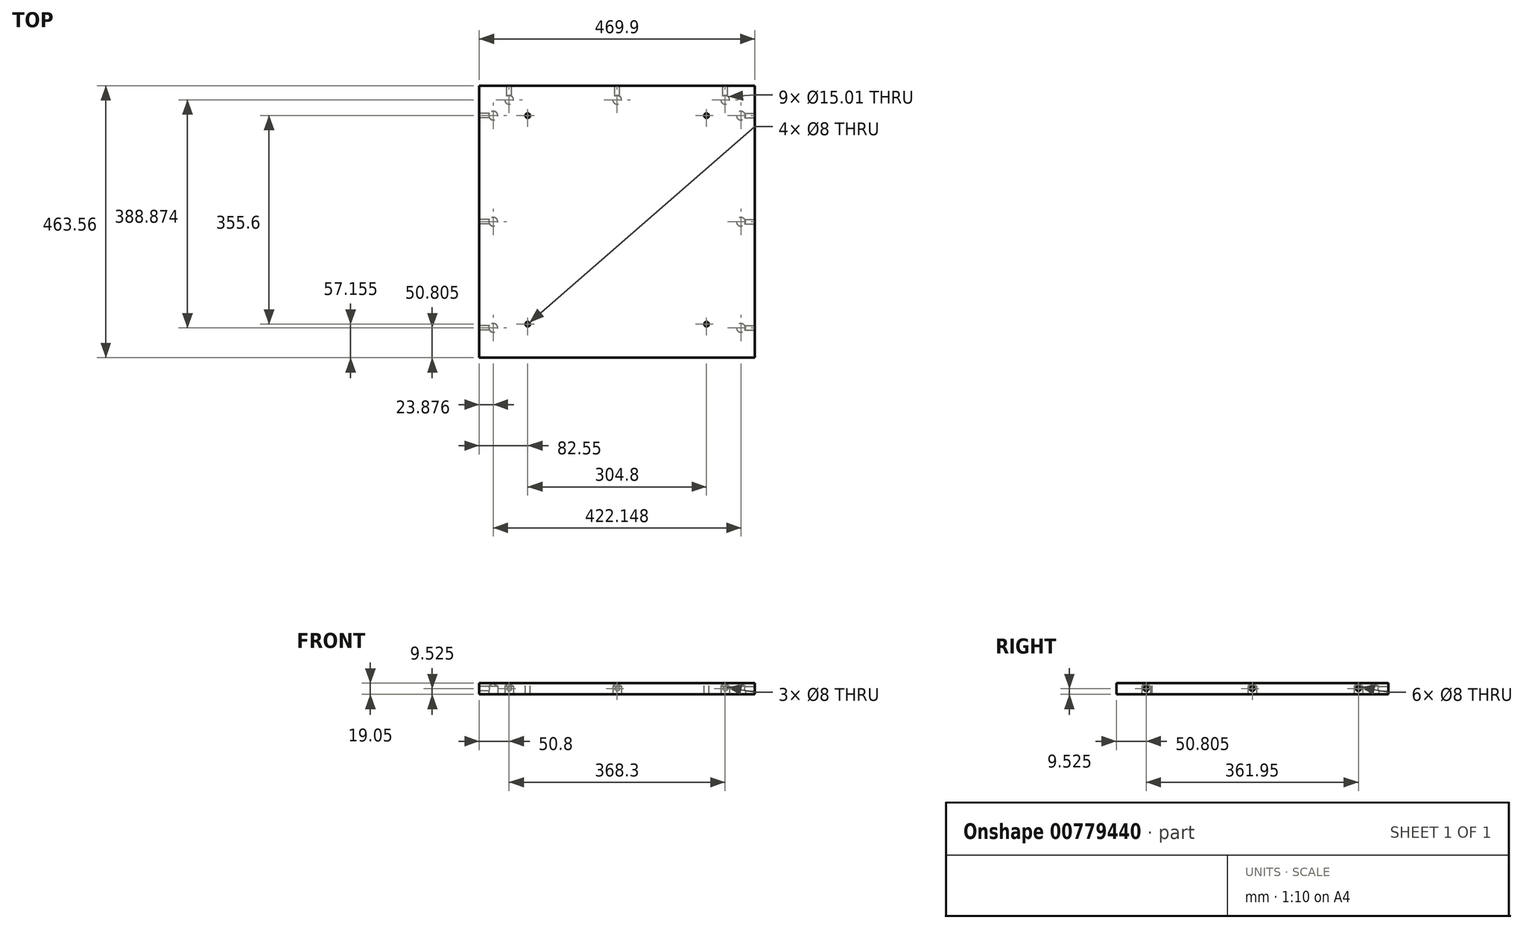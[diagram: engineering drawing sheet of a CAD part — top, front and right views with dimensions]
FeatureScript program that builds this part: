
annotation { "Feature Type Name" : "Feature", "Feature Type Description" : "" }
export const myFeature = defineFeature(function(context is Context, id is Id, definition is map)
    precondition{}
    {
        {
            var Q0;
            Q0=qCreatedBy(makeId("Top.planeOp"),FACE);
            var sketch = newSketch(context, id + "F0", { "sketchPlane" : qUnion([Q0])});
            skLineSegment(sketch, "E0.bottom", {"start": v(234.95, 231.78) * mm, "end": v(-234.95, 231.78) * mm});
            skLineSegment(sketch, "E0.top", {"start": v(234.95, -231.78) * mm, "end": v(-234.95, -231.78) * mm});
            skLineSegment(sketch, "E0.left", {"start": v(234.95, 231.77) * mm, "end": v(234.95, -231.78) * mm});
            skLineSegment(sketch, "E0.right", {"start": v(-234.95, 231.78) * mm, "end": v(-234.95, -231.78) * mm});
            skPoint(sketch, "E0.middle", {"position": v(0, 0) * mm});
            skSolve(sketch);
        }
        {
            var Q0;
            Q0=makeQuery(id+"F0.imprint","IMPRINT",FACE,{"disambiguationData":[TD([[makeQuery(id+"F0.imprint","IMPRINT",EDGE,{"derivedFrom":sQuery(id+"F0.wireOp",EDGE,"E0.bottom")}),1.0]])]});
            extrude(context, id + "F1", {"entities" : qUnion([Q0]), "depth" : 19.05 * mm, "offsetDistance" : 25.4 * mm});
        }
        {
            var Q0;
            Q0=makeQuery(id+"F1.opExtrude","CAP_FACE",FACE,{"disambiguationData":[OSD([sQuery(id+"F0.wireOp",EDGE,"E0.bottom"),sQuery(id+"F0.wireOp",EDGE,"E0.top"),sQuery(id+"F0.wireOp",EDGE,"E0.left"),sQuery(id+"F0.wireOp",EDGE,"E0.right")])],"isStart":true});
            var sketch = newSketch(context, id + "F2", { "sketchPlane" : qUnion([Q0])});
            skLineSegment(sketch, "E1", {"start": v(-234.95, 231.78) * mm, "end": v(-211.07, 231.78) * mm});
            skLineSegment(sketch, "E2", {"start": v(-211.07, 231.78) * mm, "end": v(-211.07, 180.97) * mm});
            skLineSegment(sketch, "E3", {"start": v(-234.95, -231.78) * mm, "end": v(-211.07, -231.78) * mm});
            skLineSegment(sketch, "E4", {"start": v(-211.07, -231.78) * mm, "end": v(-211.07, -180.97) * mm});
            skLineSegment(sketch, "E5", {"start": v(234.95, 231.78) * mm, "end": v(234.95, 207.9) * mm});
            skLineSegment(sketch, "E6", {"start": v(234.95, 231.78) * mm, "end": v(211.07, 231.78) * mm});
            skLineSegment(sketch, "E7", {"start": v(211.07, 231.78) * mm, "end": v(211.07, 180.97) * mm});
            skLineSegment(sketch, "E8", {"start": v(234.95, -231.78) * mm, "end": v(211.07, -231.78) * mm});
            skLineSegment(sketch, "E9", {"start": v(211.07, -231.78) * mm, "end": v(211.07, -180.97) * mm});
            skLineSegment(sketch, "E10", {"start": v(-234.95, 0) * mm, "end": v(-211.07, 0) * mm});
            skLineSegment(sketch, "E11", {"start": v(234.95, 0) * mm, "end": v(211.07, 0) * mm});
            skLineSegment(sketch, "E12", {"start": v(0, -231.78) * mm, "end": v(0, -207.9) * mm});
            skLineSegment(sketch, "E13", {"start": v(-234.95, -231.78) * mm, "end": v(-234.95, -207.9) * mm});
            skLineSegment(sketch, "E14", {"start": v(-234.95, -207.9) * mm, "end": v(-184.15, -207.9) * mm});
            skLineSegment(sketch, "E15", {"start": v(234.95, -231.78) * mm, "end": v(234.95, -207.9) * mm});
            skLineSegment(sketch, "E16", {"start": v(234.95, -207.9) * mm, "end": v(184.15, -207.9) * mm});
            skPoint(sketch, "E17", {"position": v(-211.07, 180.97) * mm});
            skPoint(sketch, "E18", {"position": v(211.07, 180.97) * mm});
            skPoint(sketch, "E19", {"position": v(211.07, 0) * mm});
            skPoint(sketch, "E20", {"position": v(-211.07, 0) * mm});
            skPoint(sketch, "E21", {"position": v(-211.07, -180.97) * mm});
            skPoint(sketch, "E22", {"position": v(-184.15, -207.9) * mm});
            skPoint(sketch, "E23", {"position": v(0, -207.9) * mm});
            skPoint(sketch, "E24", {"position": v(184.15, -207.9) * mm});
            skPoint(sketch, "E25", {"position": v(211.07, -180.97) * mm});
            skSolve(sketch);
        }
        {
            var Q0;
            Q0=sQuery(id+"F2.wireOp",VERTEX,"E17");
            var Q1;
            Q1=sQuery(id+"F2.wireOp",VERTEX,"E20");
            var Q2;
            Q2=sQuery(id+"F2.wireOp",VERTEX,"E21");
            var Q3;
            Q3=sQuery(id+"F2.wireOp",VERTEX,"E22");
            var Q4;
            Q4=sQuery(id+"F2.wireOp",VERTEX,"E23");
            var Q5;
            Q5=sQuery(id+"F2.wireOp",VERTEX,"E24");
            var Q6;
            Q6=sQuery(id+"F2.wireOp",VERTEX,"E25");
            var Q7;
            Q7=sQuery(id+"F2.wireOp",VERTEX,"E19");
            var Q8;
            Q8=sQuery(id+"F2.wireOp",VERTEX,"E18");
            var Q9;
            Q9=makeQuery(id+"F1.opExtrude","SWEPT_BODY",BODY,{"disambiguationData":[OSD([sQuery(id+"F0.wireOp",EDGE,"E0.bottom"),sQuery(id+"F0.wireOp",EDGE,"E0.top"),sQuery(id+"F0.wireOp",EDGE,"E0.left"),sQuery(id+"F0.wireOp",EDGE,"E0.right")])]});
            hole(context, id + "F3", {"style" : HoleStyle.SIMPLE, "endStyle" : HoleEndStyle.BLIND, "holeDiameter" : 15 * mm, "majorDiameter" : 6.35 * mm, "holeDepth" : 14.22 * mm, "isTappedThrough" : true, "tappedDepth" : 12.7 * mm, "tapClearance" : 3, "startFromSketch" : true, "locations" : qUnion([Q0, Q1, Q2, Q3, Q4, Q5, Q6, Q7, Q8]), "scope" : qUnion([Q9])});
        }
        {
            var Q0;
            Q0=makeQuery(id+"F1.opExtrude","SWEPT_FACE",FACE,{"disambiguationData":[OSD([sQuery(id+"F0.wireOp",EDGE,"E0.left")])]});
            var sketch = newSketch(context, id + "F4", { "sketchPlane" : qUnion([Q0])});
            skLineSegment(sketch, "E26", {"start": v(-231.77, 9.53) * mm, "end": v(-180.97, 9.53) * mm});
            skLineSegment(sketch, "E27", {"start": v(231.78, 9.53) * mm, "end": v(180.98, 9.53) * mm});
            skLineSegment(sketch, "E28", {"start": v(0, 19.05) * mm, "end": v(0, 9.53) * mm});
            skPoint(sketch, "E29", {"position": v(-180.97, 9.53) * mm});
            skPoint(sketch, "E30", {"position": v(0, 9.53) * mm});
            skPoint(sketch, "E31", {"position": v(180.98, 9.53) * mm});
            skSolve(sketch);
        }
        {
            var Q0;
            Q0=sQuery(id+"F4.wireOp",VERTEX,"E29");
            var Q1;
            Q1=sQuery(id+"F4.wireOp",VERTEX,"E30");
            var Q2;
            Q2=sQuery(id+"F4.wireOp",VERTEX,"E31");
            var Q3;
            Q3=makeQuery(id+"F1.opExtrude","SWEPT_BODY",BODY,{"disambiguationData":[OSD([sQuery(id+"F0.wireOp",EDGE,"E0.bottom"),sQuery(id+"F0.wireOp",EDGE,"E0.top"),sQuery(id+"F0.wireOp",EDGE,"E0.left"),sQuery(id+"F0.wireOp",EDGE,"E0.right")])]});
            hole(context, id + "F5", {"style" : HoleStyle.SIMPLE, "endStyle" : HoleEndStyle.BLIND, "holeDiameter" : 8 * mm, "majorDiameter" : 6.35 * mm, "holeDepth" : 25.4 * mm, "isTappedThrough" : true, "tappedDepth" : 12.7 * mm, "tapClearance" : 3, "startFromSketch" : true, "locations" : qUnion([Q0, Q1, Q2]), "scope" : qUnion([Q3])});
        }
        {
            var Q0;
            Q0=makeQuery(id+"F1.opExtrude","SWEPT_FACE",FACE,{"disambiguationData":[OSD([sQuery(id+"F0.wireOp",EDGE,"E0.bottom")])]});
            var sketch = newSketch(context, id + "F6", { "sketchPlane" : qUnion([Q0])});
            skLineSegment(sketch, "E32", {"start": v(-234.95, 9.53) * mm, "end": v(-184.15, 9.53) * mm});
            skLineSegment(sketch, "E33", {"start": v(234.95, 9.53) * mm, "end": v(184.15, 9.53) * mm});
            skLineSegment(sketch, "E34", {"start": v(0, 19.05) * mm, "end": v(0, 9.53) * mm});
            skPoint(sketch, "E35", {"position": v(-184.15, 9.53) * mm});
            skPoint(sketch, "E36", {"position": v(0, 9.53) * mm});
            skPoint(sketch, "E37", {"position": v(184.15, 9.53) * mm});
            skSolve(sketch);
        }
        {
            var Q0;
            Q0=sQuery(id+"F6.wireOp",VERTEX,"E35");
            var Q1;
            Q1=sQuery(id+"F6.wireOp",VERTEX,"E36");
            var Q2;
            Q2=sQuery(id+"F6.wireOp",VERTEX,"E37");
            var Q3;
            Q3=makeQuery(id+"F1.opExtrude","SWEPT_BODY",BODY,{"disambiguationData":[OSD([sQuery(id+"F0.wireOp",EDGE,"E0.bottom"),sQuery(id+"F0.wireOp",EDGE,"E0.top"),sQuery(id+"F0.wireOp",EDGE,"E0.left"),sQuery(id+"F0.wireOp",EDGE,"E0.right")])]});
            hole(context, id + "F7", {"style" : HoleStyle.SIMPLE, "endStyle" : HoleEndStyle.BLIND, "holeDiameter" : 8 * mm, "majorDiameter" : 6.35 * mm, "holeDepth" : 25.4 * mm, "isTappedThrough" : true, "tappedDepth" : 12.7 * mm, "tapClearance" : 3, "startFromSketch" : true, "locations" : qUnion([Q0, Q1, Q2]), "scope" : qUnion([Q3])});
        }
        {
            var Q0;
            Q0=makeQuery(id+"F1.opExtrude","SWEPT_FACE",FACE,{"disambiguationData":[OSD([sQuery(id+"F0.wireOp",EDGE,"E0.right")])]});
            var sketch = newSketch(context, id + "F8", { "sketchPlane" : qUnion([Q0])});
            skLineSegment(sketch, "E38", {"start": v(-231.77, 9.53) * mm, "end": v(-180.97, 9.53) * mm});
            skLineSegment(sketch, "E39", {"start": v(231.78, 9.53) * mm, "end": v(180.98, 9.53) * mm});
            skLineSegment(sketch, "E40", {"start": v(0, 19.05) * mm, "end": v(0, 9.53) * mm});
            skPoint(sketch, "E41", {"position": v(-180.97, 9.53) * mm});
            skPoint(sketch, "E42", {"position": v(0, 9.53) * mm});
            skPoint(sketch, "E43", {"position": v(180.98, 9.53) * mm});
            skSolve(sketch);
        }
        {
            var Q0;
            Q0=sQuery(id+"F8.wireOp",VERTEX,"E41");
            var Q1;
            Q1=sQuery(id+"F8.wireOp",VERTEX,"E42");
            var Q2;
            Q2=sQuery(id+"F8.wireOp",VERTEX,"E43");
            var Q3;
            Q3=makeQuery(id+"F1.opExtrude","SWEPT_BODY",BODY,{"disambiguationData":[OSD([sQuery(id+"F0.wireOp",EDGE,"E0.bottom"),sQuery(id+"F0.wireOp",EDGE,"E0.top"),sQuery(id+"F0.wireOp",EDGE,"E0.left"),sQuery(id+"F0.wireOp",EDGE,"E0.right")])]});
            hole(context, id + "F9", {"style" : HoleStyle.SIMPLE, "endStyle" : HoleEndStyle.BLIND, "holeDiameter" : 8 * mm, "majorDiameter" : 6.35 * mm, "holeDepth" : 25.4 * mm, "isTappedThrough" : true, "tappedDepth" : 12.7 * mm, "tapClearance" : 3, "startFromSketch" : true, "locations" : qUnion([Q0, Q1, Q2]), "scope" : qUnion([Q3])});
        }
        {
            var Q0;
            Q0=makeQuery(id+"F1.opExtrude","CAP_FACE",FACE,{"disambiguationData":[OSD([sQuery(id+"F0.wireOp",EDGE,"E0.bottom"),sQuery(id+"F0.wireOp",EDGE,"E0.top"),sQuery(id+"F0.wireOp",EDGE,"E0.left"),sQuery(id+"F0.wireOp",EDGE,"E0.right")])],"isStart":false});
            var sketch = newSketch(context, id + "F10", { "sketchPlane" : qUnion([Q0])});
            skLineSegment(sketch, "E44", {"start": v(0, 231.78) * mm, "end": v(0, 180.97) * mm});
            skLineSegment(sketch, "E45.bottom", {"start": v(0, 180.97) * mm, "end": v(-152.4, 180.97) * mm});
            skLineSegment(sketch, "E45.top", {"start": v(0, -174.63) * mm, "end": v(-152.4, -174.63) * mm});
            skLineSegment(sketch, "E45.left", {"start": v(0, 180.97) * mm, "end": v(0, -174.63) * mm});
            skLineSegment(sketch, "E45.right", {"start": v(-152.4, 180.97) * mm, "end": v(-152.4, -174.63) * mm});
            skLineSegment(sketch, "E46.bottom", {"start": v(0, 180.97) * mm, "end": v(152.4, 180.97) * mm});
            skLineSegment(sketch, "E46.top", {"start": v(0, -174.63) * mm, "end": v(152.4, -174.63) * mm});
            skLineSegment(sketch, "E46.right", {"start": v(152.4, 180.97) * mm, "end": v(152.4, -174.62) * mm});
            skPoint(sketch, "E47", {"position": v(-152.4, 180.97) * mm});
            skPoint(sketch, "E48", {"position": v(152.4, 180.97) * mm});
            skPoint(sketch, "E49", {"position": v(152.4, -174.63) * mm});
            skPoint(sketch, "E50", {"position": v(-152.4, -174.63) * mm});
            skSolve(sketch);
        }
        {
            var Q0;
            Q0=sQuery(id+"F10.wireOp",VERTEX,"E47");
            var Q1;
            Q1=sQuery(id+"F10.wireOp",VERTEX,"E48");
            var Q2;
            Q2=sQuery(id+"F10.wireOp",VERTEX,"E49");
            var Q3;
            Q3=sQuery(id+"F10.wireOp",VERTEX,"E50");
            var Q4;
            Q4=makeQuery(id+"F1.opExtrude","SWEPT_BODY",BODY,{"disambiguationData":[OSD([sQuery(id+"F0.wireOp",EDGE,"E0.bottom"),sQuery(id+"F0.wireOp",EDGE,"E0.top"),sQuery(id+"F0.wireOp",EDGE,"E0.left"),sQuery(id+"F0.wireOp",EDGE,"E0.right")])]});
            hole(context, id + "F11", {"style" : HoleStyle.SIMPLE, "endStyle" : HoleEndStyle.BLIND, "holeDiameter" : 8 * mm, "majorDiameter" : 6.35 * mm, "holeDepth" : 19.05 * mm, "isTappedThrough" : true, "tappedDepth" : 12.7 * mm, "tapClearance" : 3, "startFromSketch" : true, "locations" : qUnion([Q0, Q1, Q2, Q3]), "scope" : qUnion([Q4])});
        }
    });
